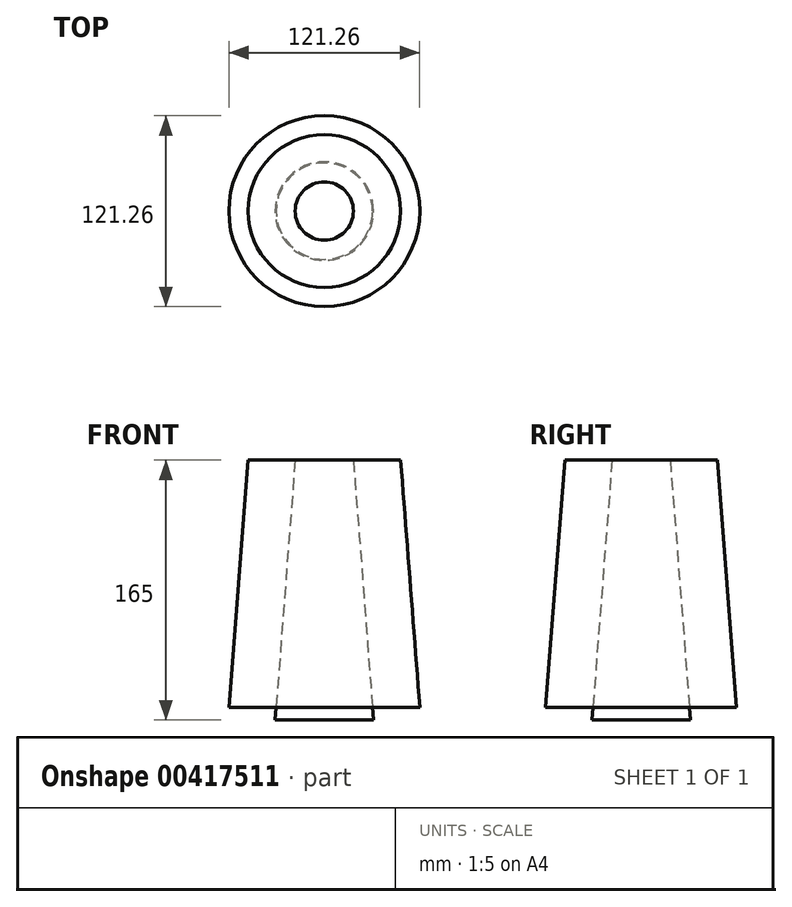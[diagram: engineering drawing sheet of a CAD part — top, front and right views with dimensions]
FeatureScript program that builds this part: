
annotation { "Feature Type Name" : "Feature", "Feature Type Description" : "" }
export const myFeature = defineFeature(function(context is Context, id is Id, definition is map)
    precondition{}
    {
        {
            var Q0;
            Q0=qCreatedBy(makeId("Front.planeOp"),FACE);
            var sketch = newSketch(context, id + "F0", { "sketchPlane" : qUnion([Q0])});
            skLineSegment(sketch, "E0", {"start": v(0, 0) * mm, "end": v(-31.25, 0) * mm});
            skLineSegment(sketch, "E1", {"start": v(-31.25, 0) * mm, "end": v(-18.5, 165) * mm});
            skLineSegment(sketch, "E2", {"start": v(-18.5, 165) * mm, "end": v(0, 165) * mm});
            skLineSegment(sketch, "E3", {"start": v(0, 165) * mm, "end": v(0, 0) * mm});
            skSolve(sketch);
        }
        {
            var Q0;
            Q0=makeQuery(id+"F0.imprint","IMPRINT",FACE,{"disambiguationData":[TD([[makeQuery(id+"F0.imprint","IMPRINT",EDGE,{"derivedFrom":sQuery(id+"F0.wireOp",EDGE,"E0")}),-1.0]])]});
            var Q1;
            Q1=sQuery(id+"F0.wireOp",EDGE,"E3");
            revolve(context, id + "F1", {"entities" : qUnion([Q0]), "axis" : qUnion([Q1]), "revolveType" : RevolveType.FULL});
        }
        {
            var Q0;
            Q0=qCreatedBy(makeId("Front.planeOp"),FACE);
            var sketch = newSketch(context, id + "F2", { "sketchPlane" : qUnion([Q0])});
            skLineSegment(sketch, "E4", {"start": v(0, 8) * mm, "end": v(-60.63, 8) * mm});
            skLineSegment(sketch, "E5", {"start": v(-60.63, 8) * mm, "end": v(-48.5, 165) * mm});
            skLineSegment(sketch, "E6", {"start": v(-48.5, 165) * mm, "end": v(0, 165) * mm});
            skLineSegment(sketch, "E7", {"start": v(0, 165) * mm, "end": v(0, 8) * mm});
            skLineSegment(sketch, "E8.0", {"start": v(-18.5, 165) * mm, "end": v(18.5, 165) * mm});
            skLineSegment(sketch, "E8.1", {"start": v(-31.25, 0) * mm, "end": v(31.25, 0) * mm});
            skLineSegment(sketch, "E9.0", {"start": v(-31.25, 0) * mm, "end": v(-18.5, 165) * mm});
            skPoint(sketch, "E10", {"position": v(-30.63, 8) * mm});
            skSolve(sketch);
        }
        {
            var Q0;
            {var subQ0=sQuery(id+"F2.wireOp",EDGE,"E5");Q0=makeQuery(id+"F2.imprint","IMPRINT",FACE,{"disambiguationData":[TD([[makeQuery(id+"F2.imprint","IMPRINT",EDGE,{"derivedFrom":subQ0}),-1.0]])]});}
            var Q1;
            Q1=sQuery(id+"F2.wireOp",EDGE,"E7");
            revolve(context, id + "F3", {"entities" : qUnion([Q0]), "axis" : qUnion([Q1]), "revolveType" : RevolveType.FULL});
        }
    });
